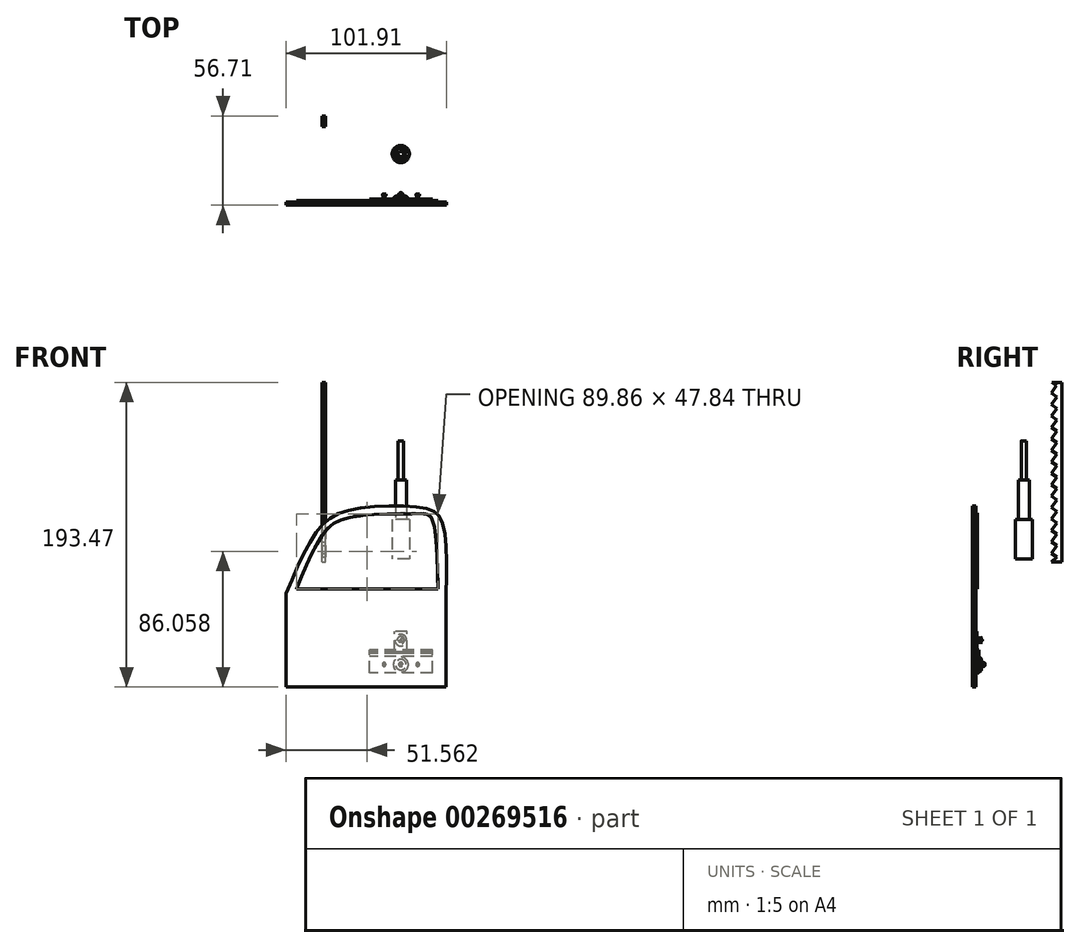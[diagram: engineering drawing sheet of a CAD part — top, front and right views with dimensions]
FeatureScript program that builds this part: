
annotation { "Feature Type Name" : "Feature", "Feature Type Description" : "" }
export const myFeature = defineFeature(function(context is Context, id is Id, definition is map)
    precondition{}
    {
        {
            var Q0;
            Q0=qCreatedBy(makeId("Front.planeOp"),FACE);
            var sketch = newSketch(context, id + "F0", { "sketchPlane" : qUnion([Q0])});
            skLineSegment(sketch, "E0.bottom", {"start": v(28.62, -81.37) * mm, "end": v(-72.94, -81.37) * mm});
            skLineSegment(sketch, "E0.left", {"start": v(28.62, -81.37) * mm, "end": v(28.62, -22.05) * mm});
            skLineSegment(sketch, "E0.right", {"start": v(-72.94, -81.37) * mm, "end": v(-72.94, -22.05) * mm});
            skFitSpline(sketch, "E1", {"points": [v(-72.94, -22.05) * mm, v(-52.29, 18.69) * mm, v(-31.26, 31.27) * mm, v(13.98, 32.4) * mm, v(25.8, 24.7) * mm, v(28.62, -22.05) * mm], "startDerivative": vector(85.44, 201.79) * mm, "endDerivative": vector(-6.45, -241.46) * mm});
            skFitSpline(sketch, "E2", {"points": [v(-66.3, -19.04) * mm, v(-48.72, 16.62) * mm, v(-31.26, 26.57) * mm, v(11.54, 28.64) * mm, v(20.36, 24.32) * mm, v(23.55, -19.23) * mm, v(23.55, -19.42) * mm], "startDerivative": vector(74.67, 181.05) * mm, "endDerivative": vector(0.05, -3.93) * mm});
            skLineSegment(sketch, "E3", {"start": v(-66.3, -19.04) * mm, "end": v(23.55, -19.23) * mm});
            skSolve(sketch);
        }
        {
            var Q0;
            Q0=makeQuery(id+"F0.imprint","IMPRINT",FACE,{"disambiguationData":[TD([[makeQuery(id+"F0.imprint","IMPRINT",EDGE,{"derivedFrom":sQuery(id+"F0.wireOp",EDGE,"E0.bottom")}),-1.0]])]});
            var Q1;
            Q1=makeQuery(id+"F0.imprint","IMPRINT",FACE,{"disambiguationData":[TD([[makeQuery(id+"F0.imprint","IMPRINT",EDGE,{"derivedFrom":sQuery(id+"F0.wireOp",EDGE,"UIrI5waD-Pjwz-Hmjb-fkDX-1jexeotdMPTl.bottom")}),1.0]])]});
            var Q2;
            Q2=qConstructionFilter(qBodyType(qCreatedBy(id+"F0",EDGE),BodyType.WIRE),ConstructionObject.NO);
            extrude(context, id + "F1", {"entities" : qUnion([Q0, Q1]), "surfaceEntities" : qUnion([Q2]), "depth" : 2 * mm});
        }
        {
            var Q0;
            Q0=makeQuery(id+"F1.opExtrude","CAP_FACE",FACE,{"disambiguationData":[OSD([sQuery(id+"F0.wireOp",EDGE,"E0.bottom"),sQuery(id+"F0.wireOp",EDGE,"E0.left"),sQuery(id+"F0.wireOp",EDGE,"E0.right"),sQuery(id+"F0.wireOp",EDGE,"E1"),sQuery(id+"F0.wireOp",EDGE,"E2"),sQuery(id+"F0.wireOp",EDGE,"E3")])],"isStart":true});
            var sketch = newSketch(context, id + "F2", { "sketchPlane" : qUnion([Q0])});
            skLineSegment(sketch, "E4", {"start": v(66.3, -19.04) * mm, "end": v(-23.55, -19.23) * mm});
            skFitSpline(sketch, "E5", {"points": [v(-23.55, -19.23) * mm, v(-22, 16.14) * mm, v(-19.49, 26.26) * mm, v(-14.23, 28.67) * mm, v(29.92, 26.8) * mm, v(44.38, 21.19) * mm, v(55.39, 5.68) * mm, v(63.63, -12.57) * mm, v(66.3, -19.04) * mm], "startDerivative": vector(4.8, 225.63) * mm, "endDerivative": vector(30.03, -71) * mm});
            skPoint(sketch, "E6.start.orphan", {"position": v(57.04, -62.16) * mm});
            skSolve(sketch);
        }
        {
            var Q0;
            Q0=qSketchRegion(id+"F2",true);
            extrude(context, id + "F3", {"entities" : qUnion([Q0]), "depth" : 1 * mm});
        }
        {
            var Q0;
            Q0=qCreatedBy(makeId("Right.planeOp"),FACE);
            var sketch = newSketch(context, id + "F4", { "sketchPlane" : qUnion([Q0])});
            skLineSegment(sketch, "E7.bottom", {"start": v(-1.09, -72.45) * mm, "end": v(-0.22, -72.45) * mm});
            skLineSegment(sketch, "E7.top", {"start": v(-1.09, -57.88) * mm, "end": v(0, -57.88) * mm});
            skLineSegment(sketch, "E7.left", {"start": v(-1.09, -72.45) * mm, "end": v(-1.09, -57.88) * mm});
            skLineSegment(sketch, "E7.right", {"start": v(2.05, -72.45) * mm, "end": v(2.05, -57.88) * mm});
            skLineSegment(sketch, "E8", {"start": v(-0.22, -72.45) * mm, "end": v(-0.22, -61.9) * mm});
            skLineSegment(sketch, "E9", {"start": v(-0.22, -61.9) * mm, "end": v(1.26, -61.9) * mm});
            skLineSegment(sketch, "E10", {"start": v(1.26, -61.9) * mm, "end": v(1.26, -72.45) * mm});
            skLineSegment(sketch, "E11.trimOffspring", {"start": v(1.26, -72.45) * mm, "end": v(2.05, -72.45) * mm});
            skLineSegment(sketch, "E12", {"start": v(0, -57.88) * mm, "end": v(0, -59.27) * mm});
            skLineSegment(sketch, "E13", {"start": v(0, -59.27) * mm, "end": v(-0.55, -59.27) * mm});
            skLineSegment(sketch, "E14", {"start": v(-0.55, -59.27) * mm, "end": v(-0.55, -60.08) * mm});
            skLineSegment(sketch, "E15", {"start": v(-0.55, -60.08) * mm, "end": v(1.43, -60.08) * mm});
            skLineSegment(sketch, "E16", {"start": v(1.43, -60.08) * mm, "end": v(1.43, -59.27) * mm});
            skPoint(sketch, "E16.endSnap0", {"position": v(-0.27, -59.27) * mm});
            skLineSegment(sketch, "E17", {"start": v(1.43, -59.27) * mm, "end": v(0.82, -59.27) * mm});
            skLineSegment(sketch, "E18", {"start": v(0.82, -59.27) * mm, "end": v(0.82, -57.88) * mm});
            skLineSegment(sketch, "E19.trimOffspring", {"start": v(0.82, -57.88) * mm, "end": v(2.05, -57.88) * mm});
            skLineSegment(sketch, "E20", {"start": v(0, -57.88) * mm, "end": v(0, -45.95) * mm});
            skLineSegment(sketch, "E21", {"start": v(0, -45.95) * mm, "end": v(0.82, -45.95) * mm});
            skLineSegment(sketch, "E22", {"start": v(0.82, -45.95) * mm, "end": v(0.82, -57.88) * mm});
            skSolve(sketch);
        }
        {
            var Q0;
            Q0=makeQuery(id+"F4.imprint","IMPRINT",FACE,{"disambiguationData":[TD([[makeQuery(id+"F4.imprint","IMPRINT",EDGE,{"derivedFrom":sQuery(id+"F4.wireOp",EDGE,"E7.bottom")}),1.0]])]});
            extrude(context, id + "F5", {"entities" : qUnion([Q0]), "endBound" : BoundingType.SYMMETRIC, "depth" : 40 * mm});
        }
        {
            var Q0;
            Q0=makeQuery(id+"F5.opExtrude","SWEPT_FACE",FACE,{"disambiguationData":[OSD([sQuery(id+"F4.wireOp",EDGE,"E7.right")])]});
            var sketch = newSketch(context, id + "F6", { "sketchPlane" : qUnion([Q0])});
            skCircle(sketch, "E23", {"center": v(-10.7, -67.1) * mm, "radius": 0.67 * mm});
            skCircle(sketch, "E24", {"center": v(10.58, -67.1) * mm, "radius": 0.68 * mm});
            skSolve(sketch);
        }
        {
            var Q0;
            Q0=qSketchRegion(id+"F6",true);
            extrude(context, id + "F7", {"entities" : qUnion([Q0]), "operationType" : NewBodyOperationType.ADD, "depth" : 2 * mm});
        }
        {
            var Q0;
            Q0=makeQuery(id+"F7.opExtrude","CAP_FACE",FACE,{"disambiguationData":[OSD([sQuery(id+"F6.wireOp",EDGE,"E23")])],"isStart":false});
            var sketch = newSketch(context, id + "F8", { "sketchPlane" : qUnion([Q0])});
            skCircle(sketch, "E25", {"center": v(-10.7, -67.1) * mm, "radius": 1.15 * mm});
            skCircle(sketch, "E26", {"center": v(10.6, -67.07) * mm, "radius": 1.15 * mm});
            skSolve(sketch);
        }
        {
            var Q0;
            Q0=qSketchRegion(id+"F8",true);
            extrude(context, id + "F9", {"entities" : qUnion([Q0]), "operationType" : NewBodyOperationType.ADD, "depth" : 1 * mm});
        }
        {
            var Q0;
            Q0=qCreatedBy(makeId("Right.planeOp"),FACE);
            var sketch = newSketch(context, id + "F10", { "sketchPlane" : qUnion([Q0])});
            skLineSegment(sketch, "E27.bottom", {"start": v(2.07, -62.39) * mm, "end": v(2.13, -62.39) * mm});
            skLineSegment(sketch, "E27.top", {"start": v(2.07, -67.18) * mm, "end": v(3.69, -67.18) * mm});
            skLineSegment(sketch, "E27.left", {"start": v(2.07, -62.39) * mm, "end": v(2.07, -67.18) * mm});
            skLineSegment(sketch, "E27.right", {"start": v(3.69, -63.81) * mm, "end": v(3.69, -67.18) * mm});
            skLineSegment(sketch, "E28", {"start": v(2.07, -67.18) * mm, "end": v(6.73, -67.18) * mm, "construction": true});
            skArc(sketch, "E29", {"start": v(3.69, -63.81) * mm, "mid": v(3.07, -62.93) * mm, "end": v(2.13, -62.39) * mm});
            skPoint(sketch, "E30", {"position": v(2.07, -64.78) * mm});
            skSolve(sketch);
        }
        {
            var Q0;
            Q0=makeQuery(id+"F10.imprint","IMPRINT",FACE,{"disambiguationData":[TD([[makeQuery(id+"F10.imprint","IMPRINT",EDGE,{"derivedFrom":sQuery(id+"F10.wireOp",EDGE,"E27.bottom")}),-1.0]])]});
            var Q1;
            Q1=sQuery(id+"F10.wireOp",EDGE,"E28");
            revolve(context, id + "F11", {"entities" : qUnion([Q0]), "axis" : qUnion([Q1]), "revolveType" : RevolveType.FULL});
        }
        {
            var Q0;
            Q0=qCreatedBy(makeId("Right.planeOp"),FACE);
            var sketch = newSketch(context, id + "F12", { "sketchPlane" : qUnion([Q0])});
            skArc(sketch, "E31", {"start": v(6, -67.1) * mm, "mid": v(4.64, -65.75) * mm, "end": v(3.3, -67.1) * mm});
            skLineSegment(sketch, "E32", {"start": v(2.6, -67.1) * mm, "end": v(7.1, -67.1) * mm, "construction": true});
            skLineSegment(sketch, "E33", {"start": v(3.3, -67.1) * mm, "end": v(6, -67.1) * mm});
            skSolve(sketch);
        }
        {
            var Q0;
            Q0=makeQuery(id+"F12.imprint","IMPRINT",FACE,{"disambiguationData":[TD([[makeQuery(id+"F12.imprint","IMPRINT",EDGE,{"derivedFrom":sQuery(id+"F12.wireOp",EDGE,"E31")}),1.0]])]});
            var Q1;
            Q1=sQuery(id+"F12.wireOp",EDGE,"E32");
            revolve(context, id + "F13", {"operationType" : NewBodyOperationType.ADD, "entities" : qUnion([Q0]), "axis" : qUnion([Q1]), "revolveType" : RevolveType.FULL});
        }
        {
            var Q0;
            Q0=qCreatedBy(makeId("Top.planeOp"),FACE);
            var sketch = newSketch(context, id + "F14", { "sketchPlane" : qUnion([Q0])});
            skLineSegment(sketch, "E34.bottom", {"start": v(-47.9, 49.9) * mm, "end": v(-44.35, 49.9) * mm});
            skLineSegment(sketch, "E34.top", {"start": v(-47.9, 46.35) * mm, "end": v(-44.35, 46.35) * mm});
            skLineSegment(sketch, "E34.left", {"start": v(-47.9, 49.9) * mm, "end": v(-47.9, 46.35) * mm});
            skLineSegment(sketch, "E34.right", {"start": v(-44.35, 49.9) * mm, "end": v(-44.35, 46.35) * mm});
            skSolve(sketch);
        }
        {
            var Q0;
            Q0 = qSketchRegion(id + "F14", true);
            extrude(context, id + "F15", {"entities" : qUnion([Q0]), "depth" : 110 * mm});
        }
        {
            var Q0;
            Q0=makeQuery(id+"F4.imprint","IMPRINT",FACE,{"disambiguationData":[TD([[makeQuery(id+"F4.imprint","IMPRINT",EDGE,{"derivedFrom":sQuery(id+"F4.wireOp",EDGE,"E12")}),1.0]])]});
            extrude(context, id + "F16", {"entities" : qUnion([Q0]), "endBound" : BoundingType.SYMMETRIC, "depth" : 8 * mm});
        }
        {
            var Q0;
            Q0=qCreatedBy(makeId("Top.planeOp"),FACE);
            var sketch = newSketch(context, id + "F17", { "sketchPlane" : qUnion([Q0])});
            skCircle(sketch, "E35", {"center": v(0, 30.56) * mm, "radius": 5.44 * mm});
            skSolve(sketch);
        }
        {
            var Q0;
            Q0 = qSketchRegion(id + "F17", true);
            extrude(context, id + "F18", {"entities" : qUnion([Q0]), "depth" : 25 * mm});
        }
        {
            var Q0;
            Q0=makeQuery(id+"F18.opExtrude","CAP_FACE",FACE,{"disambiguationData":[OSD([sQuery(id+"F17.wireOp",EDGE,"E35")])],"isStart":false});
            var sketch = newSketch(context, id + "F19", { "sketchPlane" : qUnion([Q0])});
            skCircle(sketch, "E36", {"center": v(0, 30.56) * mm, "radius": 3.48 * mm});
            skSolve(sketch);
        }
        {
            var Q0;
            Q0 = qSketchRegion(id + "F19", true);
            extrude(context, id + "F20", {"entities" : qUnion([Q0]), "operationType" : NewBodyOperationType.ADD, "depth" : 25 * mm});
        }
        {
            var Q0;
            Q0=makeQuery(id+"F20.opExtrude","CAP_FACE",FACE,{"disambiguationData":[OSD([sQuery(id+"F19.wireOp",EDGE,"E36")])],"isStart":false});
            var sketch = newSketch(context, id + "F21", { "sketchPlane" : qUnion([Q0])});
            skCircle(sketch, "E37", {"center": v(0, 30.56) * mm, "radius": 1.66 * mm});
            skSolve(sketch);
        }
        {
            var Q0;
            Q0 = qSketchRegion(id + "F21", true);
            extrude(context, id + "F22", {"entities" : qUnion([Q0]), "operationType" : NewBodyOperationType.ADD, "depth" : 25 * mm});
        }
        {
            var Q0;
            Q0=qCreatedBy(makeId("Right.planeOp"),FACE);
            var sketch = newSketch(context, id + "F23", { "sketchPlane" : qUnion([Q0])});
            skLineSegment(sketch, "E38", {"start": v(0.85, -47.93) * mm, "end": v(0.85, -51.65) * mm});
            skLineSegment(sketch, "E39", {"start": v(0.85, -51.65) * mm, "end": v(4.4, -51.65) * mm, "construction": true});
            skArc(sketch, "E40", {"start": v(4.4, -51.65) * mm, "mid": v(3.8, -51.05) * mm, "end": v(3.2, -51.65) * mm});
            skLineSegment(sketch, "E41", {"start": v(3.2, -51.65) * mm, "end": v(3.2, -49.36) * mm});
            skArc(sketch, "E42", {"start": v(3.2, -49.36) * mm, "mid": v(2.22, -48.32) * mm, "end": v(0.85, -47.93) * mm});
            skLineSegment(sketch, "E43", {"start": v(0.85, -51.65) * mm, "end": v(4.4, -51.65) * mm});
            skSolve(sketch);
        }
        {
            var Q0;
            {var subQ0=sQuery(id+"F23.wireOp",EDGE,"E40");Q0=makeQuery(id+"F23.imprint","IMPRINT",FACE,{"disambiguationData":[TD([[makeQuery(id+"F23.imprint","IMPRINT",EDGE,{"derivedFrom":subQ0}),1.0]])]});}
            var Q1;
            {var subQ0=sQuery(id+"F23.wireOp",EDGE,"E38");Q1=makeQuery(id+"F23.imprint","IMPRINT",FACE,{"disambiguationData":[TD([[makeQuery(id+"F23.imprint","IMPRINT",EDGE,{"derivedFrom":subQ0}),1.0]])]});}
            var Q2;
            Q2=sQuery(id+"F23.wireOp",EDGE,"E43");
            revolve(context, id + "F24", {"entities" : qUnion([Q0, Q1]), "axis" : qUnion([Q2]), "revolveType" : RevolveType.FULL});
        }
        {
            var Q0;
            Q0 = qSketchRegion(id + "F14", true);
            extrude(context, id + "F25", {"entities" : qUnion([Q0]), "operationType" : NewBodyOperationType.ADD, "depth" : 25 * mm});
        }
        {
            var Q0;
            Q0=makeQuery(id+"F15.opExtrude","SWEPT_FACE",FACE,{"disambiguationData":[OSD([sQuery(id+"F14.wireOp",EDGE,"E34.left")])]});
            var sketch = newSketch(context, id + "F26", { "sketchPlane" : qUnion([Q0])});
            skLineSegment(sketch, "E44.bottom", {"start": v(-48.1, 112.1) * mm, "end": v(-54.71, 112.1) * mm});
            skLineSegment(sketch, "E44.top", {"start": v(-48.1, -1.84) * mm, "end": v(-54.71, -1.84) * mm});
            skLineSegment(sketch, "E44.right", {"start": v(-54.71, 112.1) * mm, "end": v(-54.71, -1.84) * mm});
            skLineSegment(sketch, "E45", {"start": v(-48.1, -1.84) * mm, "end": v(-51.49, 1.15) * mm});
            skLineSegment(sketch, "E46", {"start": v(-51.49, 1.15) * mm, "end": v(-48.1, 3.48) * mm});
            skLineSegment(sketch, "E47", {"start": v(-48.1, 3.48) * mm, "end": v(-51.49, 8.41) * mm});
            skLineSegment(sketch, "E48", {"start": v(-51.49, 8.41) * mm, "end": v(-48.1, 10.75) * mm});
            skLineSegment(sketch, "E49", {"start": v(-48.1, 10.75) * mm, "end": v(-51.49, 15.68) * mm});
            skLineSegment(sketch, "E50", {"start": v(-51.49, 15.68) * mm, "end": v(-48.1, 18.01) * mm});
            skLineSegment(sketch, "E51", {"start": v(-48.1, 18.01) * mm, "end": v(-51.49, 22.94) * mm});
            skLineSegment(sketch, "E52", {"start": v(-51.49, 22.94) * mm, "end": v(-48.1, 25.28) * mm});
            skLineSegment(sketch, "E53", {"start": v(-48.1, 25.28) * mm, "end": v(-51.49, 30.2) * mm});
            skLineSegment(sketch, "E54", {"start": v(-51.49, 30.2) * mm, "end": v(-48.1, 32.54) * mm});
            skLineSegment(sketch, "E55", {"start": v(-48.1, 32.54) * mm, "end": v(-51.49, 37.47) * mm});
            skLineSegment(sketch, "E56", {"start": v(-51.49, 37.47) * mm, "end": v(-48.1, 39.81) * mm});
            skLineSegment(sketch, "E57", {"start": v(-48.1, 39.81) * mm, "end": v(-51.49, 44.74) * mm});
            skLineSegment(sketch, "E58", {"start": v(-51.49, 44.74) * mm, "end": v(-48.1, 47.08) * mm});
            skLineSegment(sketch, "E59", {"start": v(-48.1, 47.08) * mm, "end": v(-51.49, 52) * mm});
            skLineSegment(sketch, "E60", {"start": v(-51.49, 52) * mm, "end": v(-48.1, 54.34) * mm});
            skLineSegment(sketch, "E61", {"start": v(-48.1, 54.34) * mm, "end": v(-51.49, 59.27) * mm});
            skLineSegment(sketch, "E62", {"start": v(-51.49, 59.27) * mm, "end": v(-48.1, 61.6) * mm});
            skLineSegment(sketch, "E63", {"start": v(-48.1, 61.6) * mm, "end": v(-51.49, 66.53) * mm});
            skLineSegment(sketch, "E64", {"start": v(-51.49, 66.53) * mm, "end": v(-48.1, 68.87) * mm});
            skLineSegment(sketch, "E65", {"start": v(-48.1, 68.87) * mm, "end": v(-51.49, 73.8) * mm});
            skLineSegment(sketch, "E66", {"start": v(-51.49, 73.8) * mm, "end": v(-48.1, 76.14) * mm});
            skLineSegment(sketch, "E67", {"start": v(-48.1, 76.14) * mm, "end": v(-51.49, 81.06) * mm});
            skLineSegment(sketch, "E68", {"start": v(-51.49, 81.06) * mm, "end": v(-48.1, 83.4) * mm});
            skLineSegment(sketch, "E69", {"start": v(-48.1, 83.4) * mm, "end": v(-51.49, 88.33) * mm});
            skLineSegment(sketch, "E70", {"start": v(-51.49, 88.33) * mm, "end": v(-48.1, 90.67) * mm});
            skLineSegment(sketch, "E71", {"start": v(-48.1, 90.67) * mm, "end": v(-51.49, 95.6) * mm});
            skLineSegment(sketch, "E72", {"start": v(-51.49, 95.6) * mm, "end": v(-48.1, 97.93) * mm});
            skLineSegment(sketch, "E73", {"start": v(-48.1, 97.93) * mm, "end": v(-51.49, 102.86) * mm});
            skLineSegment(sketch, "E74", {"start": v(-51.49, 102.86) * mm, "end": v(-48.1, 105.2) * mm});
            skLineSegment(sketch, "E75", {"start": v(-48.1, 105.2) * mm, "end": v(-51.4, 110) * mm});
            skLineSegment(sketch, "E76", {"start": v(-51.4, 110) * mm, "end": v(-48.35, 112.1) * mm});
            skSolve(sketch);
        }
        {
            var Q0;
            Q0 = qSketchRegion(id + "F26", true);
            extrude(context, id + "F27", {"entities" : qUnion([Q0]), "depth" : 2 * mm});
        }
        {
            var Q0;
            Q0=makeQuery(id+"F15.opExtrude","SWEPT_BODY",BODY,{"disambiguationData":[OSD([sQuery(id+"F14.wireOp",EDGE,"E34.bottom"),sQuery(id+"F14.wireOp",EDGE,"E34.top"),sQuery(id+"F14.wireOp",EDGE,"E34.left"),sQuery(id+"F14.wireOp",EDGE,"E34.right")])]});
            deleteBodies(context, id + "F28", {"entities" : qUnion([Q0])});
        }
    });
